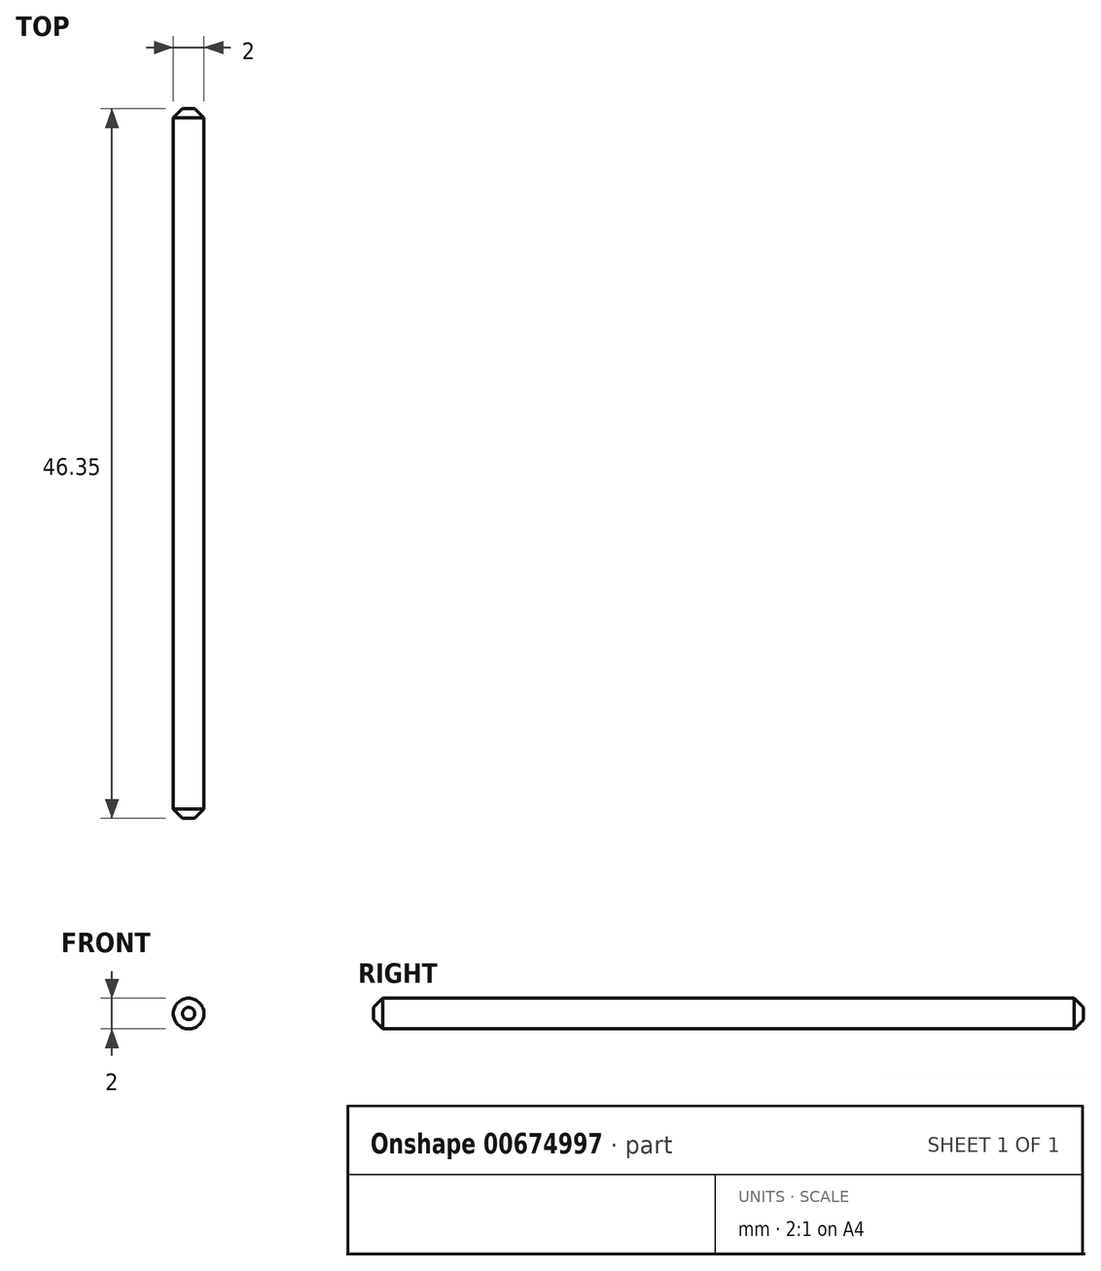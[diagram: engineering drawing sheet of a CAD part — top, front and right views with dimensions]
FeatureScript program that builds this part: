
annotation { "Feature Type Name" : "Feature", "Feature Type Description" : "" }
export const myFeature = defineFeature(function(context is Context, id is Id, definition is map)
    precondition{}
    {
        {
            assignVariable(context, id + "F0", {"name" : "Faktor", "anyValue" : 1.5});
        }
        {
            var Q0;
            Q0=qCreatedBy(makeId("Front.planeOp"),FACE);
            var sketch = newSketch(context, id + "F1", { "sketchPlane" : qUnion([Q0])});
            skCircle(sketch, "E0", {"center": v(0, 0) * mm, "radius": 1 * mm});
            skSolve(sketch);
        }
        {
            var Q0;
            Q0=qSketchRegion(id+"F1",true);
            extrude(context, id + "F2", {"entities" : qUnion([Q0]), "depth" : getVariable(context, 'Faktor') * 30.9 * mm, "offsetDistance" : 25 * mm});
        }
        {
            var Q0;
            Q0=makeQuery(id+"F2.opExtrude","CAP_EDGE",EDGE,{"disambiguationData":[OSD([sQuery(id+"F1.wireOp",EDGE,"E0")])],"isStart":false});
            var Q1;
            Q1=makeQuery(id+"F2.opExtrude","CAP_EDGE",EDGE,{"disambiguationData":[OSD([sQuery(id+"F1.wireOp",EDGE,"E0")])],"isStart":true});
            chamfer(context, id + "F3", {"entities" : qUnion([Q0, Q1]), "width" : getVariable(context, 'Faktor') * 0.4 * mm, "tangentPropagation" : true});
        }
    });
